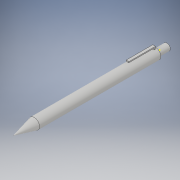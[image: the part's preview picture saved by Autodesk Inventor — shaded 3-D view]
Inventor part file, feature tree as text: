
AUTODESK INVENTOR PART (.ipt)
format: ipt  version: 2017 (Build 210142000, 142)  size: 124,928 bytes
history: native  units: in
note: dims shown in document units (in); Inventor stores cm internally (conversion verified against a paired STEP export)
features: sketch x6, other x5, extrude x4, loft x1
ambient origin geometry x8: Origin, YZ Plane, XZ Plane, XY Plane, X Axis, Y Axis, Z Axis, Center Point
bodies: Solid1 (feature_tree)
feature tree (16):
  extrude  "Pen body"  Depth=4.0in TaperAngle=0.0deg
  other  "Tip Plane"
  loft  "Body to Tip"
  sketch  "Sketch3"  dims[d5=0.0in d6=90.0deg d7=0.0in d8=90.0deg]
  extrude  "Click"  TaperAngle=0.0deg  [1 undecoded]
  other  "Clip"
  other  "Clip extention"
  other  "Clips extension's extension"
  extrude  "Extrusion3"  Depth=0.375in
  extrude  "Extrusion4"  Depth=0.83in TaperAngle=0.0deg
  sketch  "Sketch1"  dims[d0=0.35in d1=4.0in d2=0.0in]
  sketch  "Sketch2"  dims[d3=0.7in d4=0.002in]
  other  "Edges1"
  sketch  "Sketch4"  dims[d9=0.375in d10=0.0in d11=0.158in]
  sketch  "Sketch7"  dims[d12=0.08in d13=0.0in d14=0.83in d15=0.0in]
  sketch  "Sketch8"
note: 1 required parameter value undecoded (feature->parameter linkage not recoverable at this tier; creation-order binding heuristic only, values carry confidence <= 0.55)
